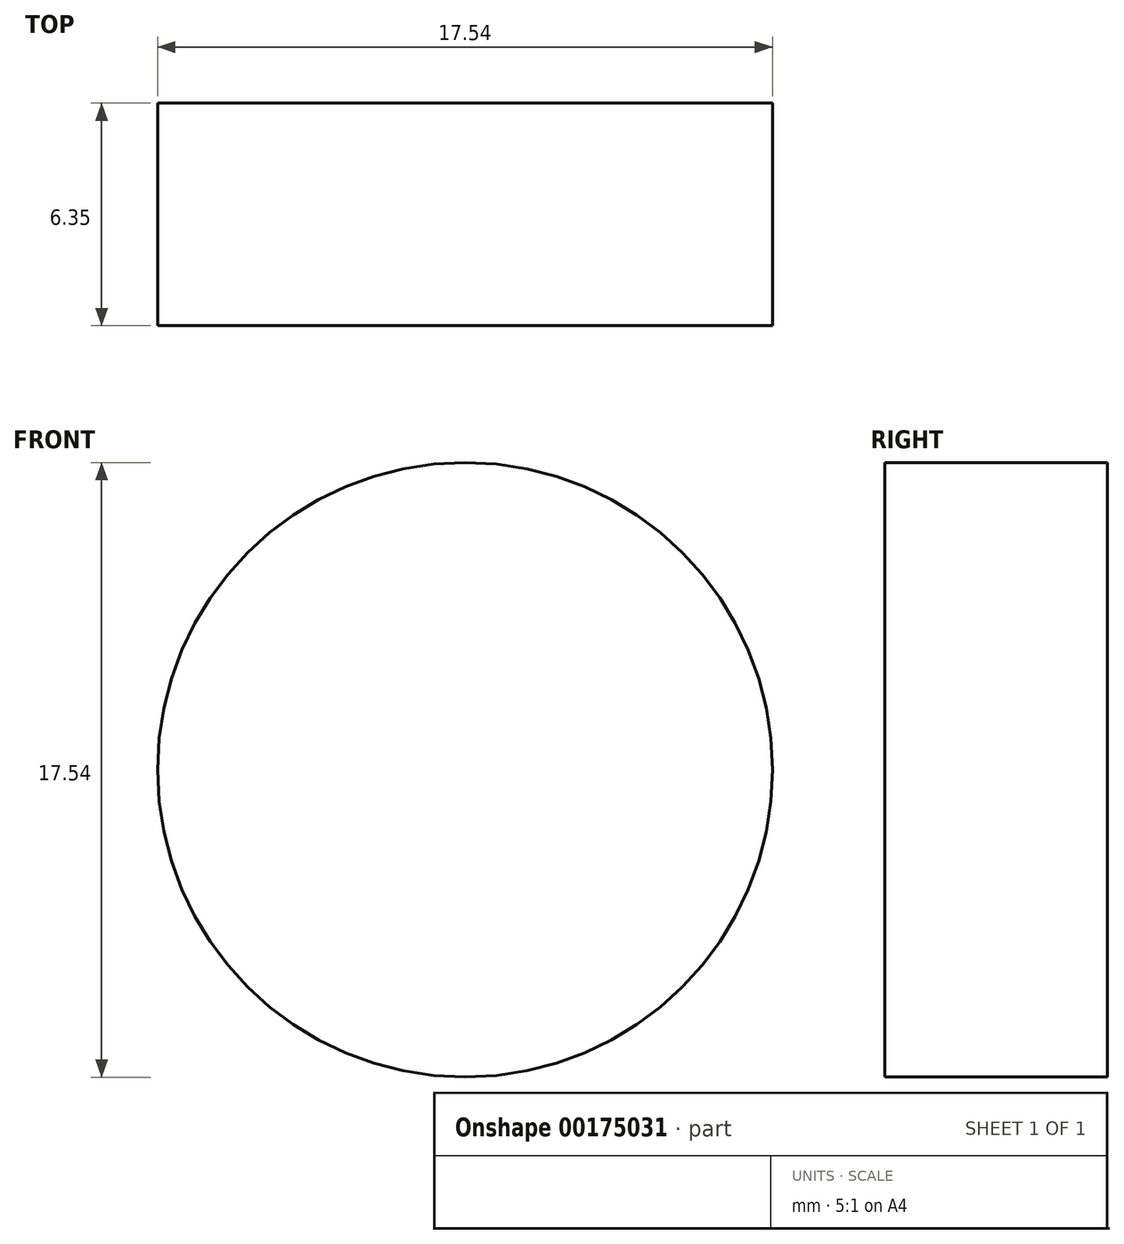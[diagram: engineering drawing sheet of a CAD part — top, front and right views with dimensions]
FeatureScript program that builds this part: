
annotation { "Feature Type Name" : "Feature", "Feature Type Description" : "" }
export const myFeature = defineFeature(function(context is Context, id is Id, definition is map)
    precondition{}
    {
        {
            var Q0;
            Q0=qCreatedBy(makeId("Front.planeOp"),FACE);
            var sketch = newSketch(context, id + "F0", { "sketchPlane" : qUnion([Q0])});
            skLineSegment(sketch, "E0", {"start": v(-50.8, 8.78) * mm, "end": v(-50.8, -35.67) * mm});
            skLineSegment(sketch, "E1", {"start": v(-50.8, -35.67) * mm, "end": v(0, -35.67) * mm});
            skLineSegment(sketch, "E2", {"start": v(-50.8, 8.78) * mm, "end": v(-15.88, 25.16) * mm});
            skLineSegment(sketch, "E3", {"start": v(-15.88, 25.16) * mm, "end": v(0, 25.16) * mm});
            skLineSegment(sketch, "E4", {"start": v(0, 25.16) * mm, "end": v(0, -35.67) * mm});
            skLineSegment(sketch, "E5.MirrorCS", {"start": v(15.88, 25.16) * mm, "end": v(0, 25.16) * mm});
            skLineSegment(sketch, "E6.MirrorCS", {"start": v(50.8, 8.78) * mm, "end": v(15.88, 25.16) * mm});
            skLineSegment(sketch, "E7.MirrorCS", {"start": v(50.8, 8.78) * mm, "end": v(50.8, -35.67) * mm});
            skLineSegment(sketch, "E8.MirrorCS", {"start": v(50.8, -35.67) * mm, "end": v(0, -35.67) * mm});
            skSolve(sketch);
        }
        {
            var Q0;
            Q0 = qSketchRegion(id + "F0", true);
            extrude(context, id + "F1", {"entities" : qUnion([Q0]), "depth" : 6.35 * mm});
        }
        {
            var Q0;
            Q0=makeQuery(id+"F1.opExtrude","CAP_FACE",FACE,{"disambiguationData":[OSD([sQuery(id+"F0.wireOp",EDGE,"E0"),sQuery(id+"F0.wireOp",EDGE,"E1"),sQuery(id+"F0.wireOp",EDGE,"E2"),sQuery(id+"F0.wireOp",EDGE,"E3"),sQuery(id+"F0.wireOp",EDGE,"E4")])],"isStart":false});
            var sketch = newSketch(context, id + "F2", { "sketchPlane" : qUnion([Q0])});
            skCircle(sketch, "E9", {"center": v(-31.75, -16.62) * mm, "radius": 8.77 * mm});
            skCircle(sketch, "E10.MirrorC", {"center": v(31.75, -16.62) * mm, "radius": 8.77 * mm});
            skCircle(sketch, "E11", {"center": v(0, -3.92) * mm, "radius": 15.88 * mm});
            skSolve(sketch);
        }
        {
            var Q0;
            {var subQ0=sQuery(id+"F2.wireOp",EDGE,"cqWXvoJt-I7Om-OUJ0-qbZi-EFLETkbDVXdr");Q0=makeQuery(id+"F2.imprint","IMPRINT",FACE,{"disambiguationData":[TD([[makeQuery(id+"F2.imprint","IMPRINT",EDGE,{"derivedFrom":subQ0}),1.0]])]});}
            var Q1;
            Q1=makeQuery(id+"F2.imprint","IMPRINT",FACE,{"disambiguationData":[TD([[makeQuery(id+"F2.imprint","IMPRINT",EDGE,{"derivedFrom":sQuery(id+"F2.wireOp",EDGE,"E11")}),1.0]])]});
            var Q2;
            Q2=makeQuery(id+"F2.imprint","IMPRINT",FACE,{"disambiguationData":[TD([[makeQuery(id+"F2.imprint","IMPRINT",EDGE,{"derivedFrom":sQuery(id+"F2.wireOp",EDGE,"E10.MirrorC")}),-1.0]])]});
            var Q3;
            Q3=makeQuery(id+"F2.imprint","IMPRINT",FACE,{"disambiguationData":[TD([[makeQuery(id+"F2.imprint","IMPRINT",EDGE,{"derivedFrom":sQuery(id+"F2.wireOp",EDGE,"E9")}),1.0]])]});
            extrude(context, id + "F3", {"entities" : qUnion([Q0, Q1, Q2, Q3]), "operationType" : NewBodyOperationType.REMOVE, "oppositeDirection" : true, "depth" : 6.35 * mm});
        }
    });
